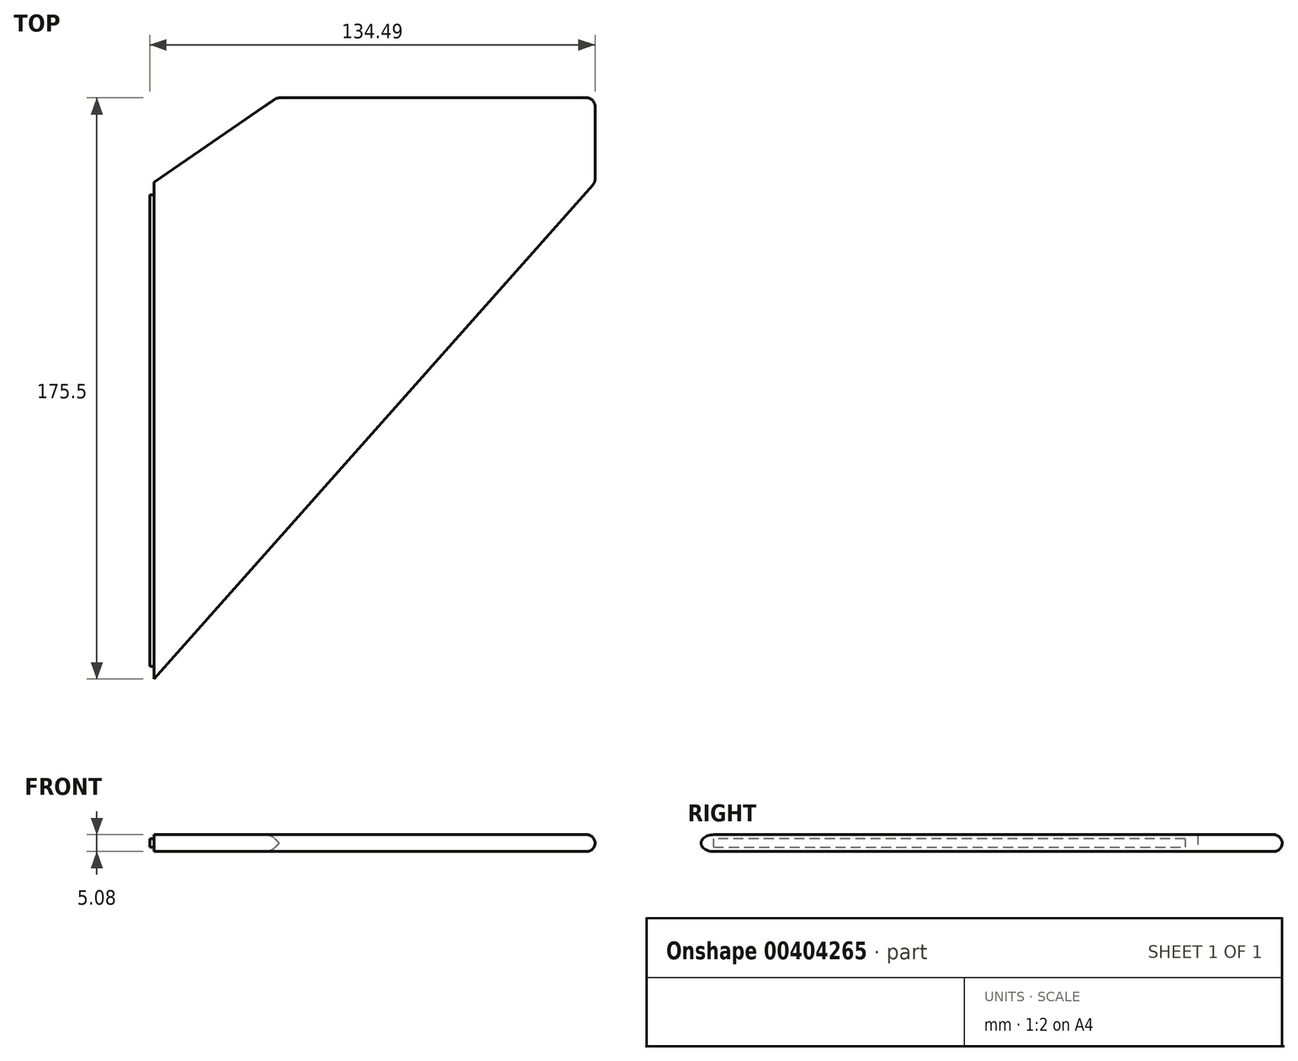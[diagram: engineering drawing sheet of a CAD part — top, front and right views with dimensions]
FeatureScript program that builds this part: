
annotation { "Feature Type Name" : "Feature", "Feature Type Description" : "" }
export const myFeature = defineFeature(function(context is Context, id is Id, definition is map)
    precondition{}
    {
        {
            var Q0;
            Q0=qCreatedBy(makeId("Front.planeOp"),FACE);
            var sketch = newSketch(context, id + "F0", { "sketchPlane" : qUnion([Q0])});
            skCircle(sketch, "E0", {"center": v(0, 0) * mm, "radius": 32.78 * mm});
            skCircle(sketch, "E1", {"center": v(0, 0) * mm, "radius": 26.47 * mm});
            skLineSegment(sketch, "E2", {"start": v(0, -76.2) * mm, "end": v(0, 76.2) * mm});
            skCircle(sketch, "E3", {"center": v(0, 0) * mm, "radius": 13.86 * mm});
            skSolve(sketch);
        }
        {
            var Q0;
            {var subQ0=sQuery(id+"F0.wireOp",EDGE,"E2");var subQ1=sQuery(id+"F0.wireOp",EDGE,"E0");var subQ2=makeQuery(id+"F0.imprint","INTERSECT",VERTEX,{"disambiguationData":[OD(1.0)],"derivedFrom":[subQ1,subQ0]});Q0=makeQuery(id+"F0.imprint","IMPRINT",FACE,{"disambiguationData":[TD([[makeQuery(id+"F0.imprint","IMPRINT",EDGE,{"disambiguationData":[TD([[subQ2,-1.0]])],"derivedFrom":subQ1}),1.0]])]});}
            var Q1;
            {var subQ0=sQuery(id+"F0.wireOp",EDGE,"E2");var subQ1=sQuery(id+"F0.wireOp",EDGE,"E0");var subQ2=makeQuery(id+"F0.imprint","INTERSECT",VERTEX,{"disambiguationData":[OD(1.0)],"derivedFrom":[subQ1,subQ0]});Q1=makeQuery(id+"F0.imprint","IMPRINT",FACE,{"disambiguationData":[TD([[makeQuery(id+"F0.imprint","IMPRINT",EDGE,{"disambiguationData":[TD([[subQ2,1.0]])],"derivedFrom":subQ1}),1.0]])]});}
            var Q2;
            {var subQ0=sQuery(id+"F0.wireOp",EDGE,"5oPWdtzy-OPul-B56H-vmQn-ATjjeZZYbcvi");var subQ1=sQuery(id+"F0.wireOp",EDGE,"E0");var subQ2=makeQuery(id+"F0.imprint","INTERSECT",VERTEX,{"disambiguationData":[OD(1.0)],"derivedFrom":[subQ1,subQ0]});Q2=makeQuery(id+"F0.imprint","IMPRINT",FACE,{"disambiguationData":[TD([[makeQuery(id+"F0.imprint","IMPRINT",EDGE,{"disambiguationData":[TD([[subQ2,-1.0]])],"derivedFrom":subQ1}),1.0]])]});}
            var Q3;
            {var subQ0=sQuery(id+"F0.wireOp",EDGE,"5oPWdtzy-OPul-B56H-vmQn-ATjjeZZYbcvi");var subQ1=sQuery(id+"F0.wireOp",EDGE,"E0");var subQ2=makeQuery(id+"F0.imprint","INTERSECT",VERTEX,{"disambiguationData":[OD(0.0)],"derivedFrom":[subQ1,subQ0]});Q3=makeQuery(id+"F0.imprint","IMPRINT",FACE,{"disambiguationData":[TD([[makeQuery(id+"F0.imprint","IMPRINT",EDGE,{"disambiguationData":[TD([[subQ2,1.0]])],"derivedFrom":subQ1}),1.0]])]});}
            var Q4;
            {var subQ0=sQuery(id+"F0.wireOp",EDGE,"E2");var subQ1=sQuery(id+"F0.wireOp",EDGE,"E0");var subQ2=makeQuery(id+"F0.imprint","INTERSECT",VERTEX,{"disambiguationData":[OD(0.0)],"derivedFrom":[subQ1,subQ0]});Q4=makeQuery(id+"F0.imprint","IMPRINT",FACE,{"disambiguationData":[TD([[makeQuery(id+"F0.imprint","IMPRINT",EDGE,{"disambiguationData":[TD([[subQ2,1.0]])],"derivedFrom":subQ1}),1.0]])]});}
            var Q5;
            {var subQ0=sQuery(id+"F0.wireOp",EDGE,"1dQYtLTc-Qprp-vLL3-yUOJ-yKbSne6VpX0o");var subQ1=sQuery(id+"F0.wireOp",EDGE,"E0");var subQ2=makeQuery(id+"F0.imprint","INTERSECT",VERTEX,{"disambiguationData":[OD(0.0)],"derivedFrom":[subQ1,subQ0]});Q5=makeQuery(id+"F0.imprint","IMPRINT",FACE,{"disambiguationData":[TD([[makeQuery(id+"F0.imprint","IMPRINT",EDGE,{"disambiguationData":[TD([[subQ2,1.0]])],"derivedFrom":subQ1}),1.0]])]});}
            var Q6;
            {var subQ0=sQuery(id+"F0.wireOp",EDGE,"E2");var subQ1=sQuery(id+"F0.wireOp",EDGE,"E0");var subQ2=makeQuery(id+"F0.imprint","INTERSECT",VERTEX,{"disambiguationData":[OD(0.0)],"derivedFrom":[subQ1,subQ0]});Q6=makeQuery(id+"F0.imprint","IMPRINT",FACE,{"disambiguationData":[TD([[makeQuery(id+"F0.imprint","IMPRINT",EDGE,{"disambiguationData":[TD([[subQ2,-1.0]])],"derivedFrom":subQ1}),1.0]])]});}
            var Q7;
            {var subQ0=sQuery(id+"F0.wireOp",EDGE,"1dQYtLTc-Qprp-vLL3-yUOJ-yKbSne6VpX0o");var subQ1=sQuery(id+"F0.wireOp",EDGE,"E0");var subQ2=makeQuery(id+"F0.imprint","INTERSECT",VERTEX,{"disambiguationData":[OD(1.0)],"derivedFrom":[subQ1,subQ0]});Q7=makeQuery(id+"F0.imprint","IMPRINT",FACE,{"disambiguationData":[TD([[makeQuery(id+"F0.imprint","IMPRINT",EDGE,{"disambiguationData":[TD([[subQ2,-1.0]])],"derivedFrom":subQ1}),1.0]])]});}
            extrude(context, id + "F1", {"entities" : qUnion([Q0, Q1, Q2, Q3, Q4, Q5, Q6, Q7]), "depth" : 171.45 * mm});
        }
        {
            var Q0;
            Q0=qCreatedBy(makeId("Top.planeOp"),FACE);
            var sketch = newSketch(context, id + "F2", { "sketchPlane" : qUnion([Q0])});
            skPoint(sketch, "E4", {"position": v(33.43, -150) * mm});
            skPoint(sketch, "E5", {"position": v(33.43, 0) * mm});
            skLineSegment(sketch, "E6", {"start": v(33.43, -150) * mm, "end": v(33.43, 0) * mm});
            skLineSegment(sketch, "E7", {"start": v(33.43, -150) * mm, "end": v(166.65, 0) * mm});
            skLineSegment(sketch, "E8", {"start": v(33.43, 0) * mm, "end": v(70.51, 25.5) * mm});
            skLineSegment(sketch, "E9", {"start": v(166.65, 0) * mm, "end": v(166.65, 25.5) * mm});
            skLineSegment(sketch, "E10", {"start": v(166.65, 25.5) * mm, "end": v(70.51, 25.5) * mm});
            skLineSegment(sketch, "E11", {"start": v(-33.46, -150) * mm, "end": v(-166.81, 0) * mm});
            skLineSegment(sketch, "E12", {"start": v(-166.81, 0) * mm, "end": v(-166.81, 25.5) * mm});
            skLineSegment(sketch, "E13", {"start": v(-166.81, 25.5) * mm, "end": v(-70.54, 25.5) * mm});
            skLineSegment(sketch, "E14", {"start": v(-70.54, 25.5) * mm, "end": v(-33.47, 0) * mm});
            skLineSegment(sketch, "E15", {"start": v(-33.47, 0) * mm, "end": v(-166.81, 0) * mm});
            skLineSegment(sketch, "E16", {"start": v(-33.47, 0) * mm, "end": v(-33.46, -150) * mm});
            skLineSegment(sketch, "E17", {"start": v(166.65, 0) * mm, "end": v(33.43, 0) * mm});
            skSolve(sketch);
        }
        {
            var Q0;
            {var subQ0=sQuery(id+"F2.wireOp",EDGE,"E8");Q0=makeQuery(id+"F2.imprint","IMPRINT",FACE,{"disambiguationData":[TD([[makeQuery(id+"F2.imprint","IMPRINT",EDGE,{"derivedFrom":subQ0}),-1.0]])]});}
            var Q1;
            {var subQ0=sQuery(id+"F2.wireOp",EDGE,"E6");Q1=makeQuery(id+"F2.imprint","IMPRINT",FACE,{"disambiguationData":[TD([[makeQuery(id+"F2.imprint","IMPRINT",EDGE,{"derivedFrom":subQ0}),-1.0]])]});}
            var Q2;
            Q2=makeQuery(id+"F2.imprint","IMPRINT",FACE,{"disambiguationData":[TD([[makeQuery(id+"F2.imprint","IMPRINT",EDGE,{"derivedFrom":sQuery(id+"F2.wireOp",EDGE,"E12")}),-1.0]])]});
            var Q3;
            Q3=makeQuery(id+"F2.imprint","IMPRINT",FACE,{"disambiguationData":[TD([[makeQuery(id+"F2.imprint","IMPRINT",EDGE,{"derivedFrom":sQuery(id+"F2.wireOp",EDGE,"E11")}),-1.0]])]});
            extrude(context, id + "F3", {"entities" : qUnion([Q0, Q1, Q2, Q3]), "operationType" : NewBodyOperationType.ADD, "endBound" : BoundingType.SYMMETRIC, "depth" : 5.08 * mm});
        }
        {
            var Q0;
            Q0=makeQuery(id+"F1.opExtrude","SWEPT_BODY",BODY,{"disambiguationData":[OSD([sQuery(id+"F0.wireOp",EDGE,"E0"),sQuery(id+"F0.wireOp",EDGE,"E1")])]});
            var Q1;
            Q1=makeQuery(id+"FjVrq8M5eGH33Nd_3.opExtrude","SWEPT_BODY",BODY,{"disambiguationData":[OSD([sQuery(id+"FK3utR1xAzgM6UN_3.wireOp",EDGE,"IUXL1Bh7-QCcG-6Ly2-nHPW-iYtw5I6giJH0"),sQuery(id+"FK3utR1xAzgM6UN_3.wireOp",EDGE,"JStxZuMw-bqw7-a8hU-d2SW-pg4xeFH4hPPH"),sQuery(id+"FK3utR1xAzgM6UN_3.wireOp",EDGE,"edqHRoiu-R6Q2-hWB9-HESb-Stfgj3zz6ipz"),sQuery(id+"FK3utR1xAzgM6UN_3.wireOp",EDGE,"3hYN0WH2-VQ0w-20pU-Acjj-TIV3PpBxMGE5"),sQuery(id+"FK3utR1xAzgM6UN_3.wireOp",EDGE,"6uPkyx4M-MP5n-rn9n-Yx59-YpWobmbrasir")])]});
            var Q2;
            Q2=makeQuery(id+"FjVrq8M5eGH33Nd_3.opExtrude","SWEPT_BODY",BODY,{"disambiguationData":[OSD([sQuery(id+"FK3utR1xAzgM6UN_3.wireOp",EDGE,"UwiaApss-JNcw-qIXk-sKKo-oQS70Patney0"),sQuery(id+"FK3utR1xAzgM6UN_3.wireOp",EDGE,"ns8jL1o4-dCT8-lhzt-NO6D-4ueuO0nmNpz3"),sQuery(id+"FK3utR1xAzgM6UN_3.wireOp",EDGE,"Vopa3ZxI-8NRL-vm1O-ylc2-mN06THWPdNrS"),sQuery(id+"FK3utR1xAzgM6UN_3.wireOp",EDGE,"uMN0t8l9-b9ac-YmP0-29np-bEfdAQuar3nl"),sQuery(id+"FK3utR1xAzgM6UN_3.wireOp",EDGE,"cIXhV6cs-eH8k-LNdS-vHhi-eNs58iRvXYyc")])]});
            deleteBodies(context, id + "F4", {"entities" : qUnion([Q0, Q1, Q2])});
        }
        {
            var Q0;
            Q0=makeQuery(id+"F3.opExtrude","SWEPT_BODY",BODY,{"disambiguationData":[OSD([sQuery(id+"F2.wireOp",EDGE,"E11"),sQuery(id+"F2.wireOp",EDGE,"E12"),sQuery(id+"F2.wireOp",EDGE,"E13"),sQuery(id+"F2.wireOp",EDGE,"E14"),sQuery(id+"F2.wireOp",EDGE,"E16")])]});
            deleteBodies(context, id + "F5", {"entities" : qUnion([Q0])});
        }
        {
            var Q0;
            Q0=makeQuery(id+"F3.opExtrude","SWEPT_FACE",FACE,{"disambiguationData":[OSD([sQuery(id+"F2.wireOp",EDGE,"E6")])]});
            var sketch = newSketch(context, id + "F6", { "sketchPlane" : qUnion([Q0])});
            skLineSegment(sketch, "E18.0", {"start": v(3.8, 1.27) * mm, "end": v(146.19, 1.27) * mm});
            skLineSegment(sketch, "E18.1", {"start": v(3.8, 1.27) * mm, "end": v(3.8, -1.27) * mm});
            skLineSegment(sketch, "E18.2", {"start": v(146.19, -1.27) * mm, "end": v(3.8, -1.27) * mm});
            skLineSegment(sketch, "E18.3", {"start": v(146.19, -1.27) * mm, "end": v(146.19, 1.27) * mm});
            skSolve(sketch);
        }
        {
            var Q0;
            Q0=makeQuery(id+"F6.imprint","IMPRINT",FACE,{"disambiguationData":[TD([[makeQuery(id+"F6.imprint","IMPRINT",EDGE,{"derivedFrom":sQuery(id+"F6.wireOp",EDGE,"E18.0")}),-1.0]])]});
            extrude(context, id + "F7", {"entities" : qUnion([Q0]), "operationType" : NewBodyOperationType.ADD, "depth" : 1.27 * mm});
        }
        {
            var Q0;
            Q0=makeQuery(id+"F3.opExtrude","SWEPT_FACE",FACE,{"disambiguationData":[OSD([sQuery(id+"F2.wireOp",EDGE,"E9")])]});
            var Q1;
            Q1=makeQuery(id+"F3.opExtrude","SWEPT_FACE",FACE,{"disambiguationData":[OSD([sQuery(id+"F2.wireOp",EDGE,"E7")])]});
            var Q2;
            Q2=makeQuery(id+"F3.opExtrude","SWEPT_FACE",FACE,{"disambiguationData":[OSD([sQuery(id+"F2.wireOp",EDGE,"E10")])]});
            fillet(context, id + "F8", {"entities" : qUnion([Q0, Q1, Q2]), "radius" : 2.54 * mm, "tangentPropagation" : true, "allowEdgeOverflow" : false});
        }
    });
